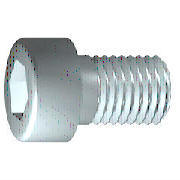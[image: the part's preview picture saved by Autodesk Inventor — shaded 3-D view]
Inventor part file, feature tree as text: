
AUTODESK INVENTOR PART (.ipt)
format: ipt  version: 2024 (Build 280153000, 153)  size: 188,416 bytes
history: native  units: mm (DEFAULTED — no unit token found)
features: fillet x2, sketch x2, extrude x1, thread x1, chamfer x1, plane x1
ambient origin geometry x7: Origin, YZ Plane, XY Plane, X Axis, Y Axis, Z Axis, Center Point
bodies: Solid1 (feature_tree), Body (feature_tree)
feature tree (8):
  extrude  "Slot"  Depth=2.0mm
  fillet  "Fillet1"  Radius=4.0mm
  thread  "Thread"  [1 undecoded]
  chamfer  "Chamfer1"  Distance=4.0mm
  plane  "Work Plane1"
  fillet  "Fillet2"  Radius=4.0mm
  sketch  "Sketch1"  dims[d1=18.25mm d2=0.429515mm d3=4.0mm d4=2.0mm]
  sketch  "Sketch2"  dims[d5=60.0deg d6=4.0mm d7=4.0mm d8=3.464102mm d9=7.0mm d10=90.0deg d11=10.0mm d12=0.0mm d13=18.25mm d14=0.0mm d15=0.429415mm d16=0.429415mm d17=0.4mm d19=0.0mm d26=20.0mm d27=45.0deg d28=0.0mm d29=0.0mm d30=0.1mm]
note: 1 required parameter value undecoded (feature->parameter linkage not recoverable at this tier; creation-order binding heuristic only, values carry confidence <= 0.55)
